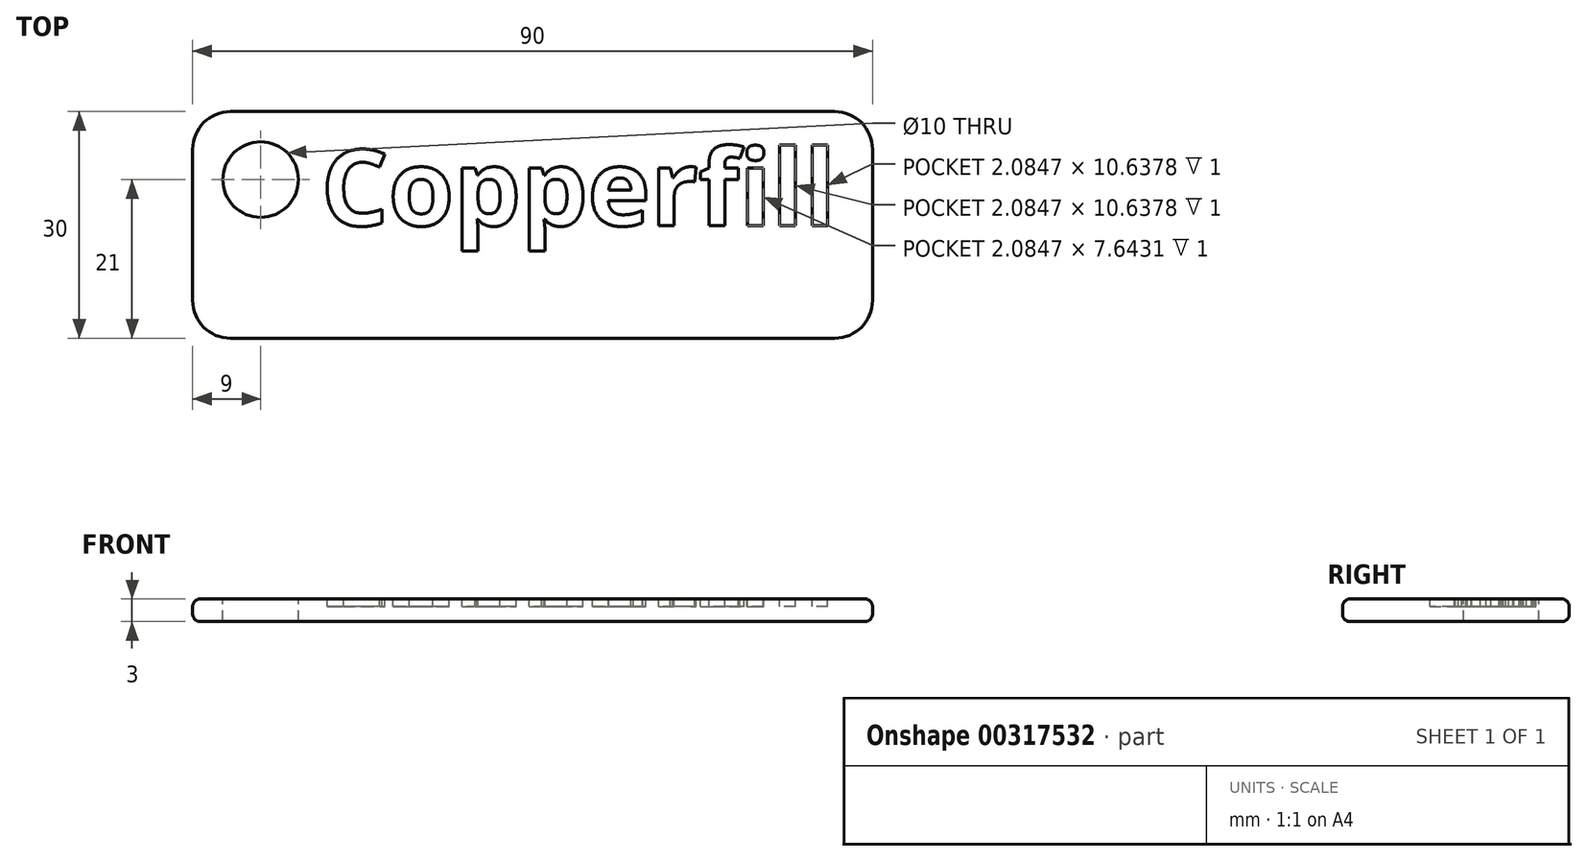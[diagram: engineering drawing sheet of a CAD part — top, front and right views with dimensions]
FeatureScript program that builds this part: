
annotation { "Feature Type Name" : "Feature", "Feature Type Description" : "" }
export const myFeature = defineFeature(function(context is Context, id is Id, definition is map)
    precondition{}
    {
        {
            var Q0;
            Q0=qCreatedBy(makeId("Top.planeOp"),FACE);
            var sketch = newSketch(context, id + "F0", { "sketchPlane" : qUnion([Q0])});
            skLineSegment(sketch, "E0.bottom", {"start": v(-45, 15) * mm, "end": v(45, 15) * mm});
            skLineSegment(sketch, "E0.top", {"start": v(-45, -15) * mm, "end": v(45, -15) * mm});
            skLineSegment(sketch, "E0.left", {"start": v(-45, 15) * mm, "end": v(-45, -15) * mm});
            skLineSegment(sketch, "E0.right", {"start": v(45, 15) * mm, "end": v(45, -15) * mm});
            skLineSegment(sketch, "E1", {"start": v(-45, 15) * mm, "end": v(45, -15) * mm, "construction": true});
            skSolve(sketch);
        }
        {
            var Q0;
            Q0=makeQuery(id+"F0.imprint","IMPRINT",FACE,{"disambiguationData":[TD([[makeQuery(id+"F0.imprint","IMPRINT",EDGE,{"derivedFrom":sQuery(id+"F0.wireOp",EDGE,"E0.bottom")}),-1.0]])]});
            extrude(context, id + "F1", {"entities" : qUnion([Q0]), "depth" : 3 * mm});
        }
        {
            var Q0;
            Q0=makeQuery(id+"F1.opExtrude","CAP_FACE",FACE,{"disambiguationData":[OSD([sQuery(id+"F0.wireOp",EDGE,"E0.bottom"),sQuery(id+"F0.wireOp",EDGE,"E0.top"),sQuery(id+"F0.wireOp",EDGE,"E0.left"),sQuery(id+"F0.wireOp",EDGE,"E0.right")])],"isStart":false});
            var Q1;
            Q1=makeQuery(id+"F1.opExtrude","CAP_FACE",FACE,{"disambiguationData":[OSD([sQuery(id+"F0.wireOp",EDGE,"E0.bottom"),sQuery(id+"F0.wireOp",EDGE,"E0.top"),sQuery(id+"F0.wireOp",EDGE,"E0.left"),sQuery(id+"F0.wireOp",EDGE,"E0.right")])],"isStart":true});
            fillet(context, id + "F2", {"entities" : qUnion([Q0, Q1]), "radius" : 1 * mm, "tangentPropagation" : true, "allowEdgeOverflow" : false});
        }
        {
            var Q0;
            Q0=makeQuery(id+"F1.opExtrude","SWEPT_EDGE",EDGE,{"disambiguationData":[OSD([sQuery(id+"F0.wireOp",EDGE,"E0.top"),sQuery(id+"F0.wireOp",EDGE,"E0.right")])]});
            var Q1;
            Q1=makeQuery(id+"F1.opExtrude","SWEPT_EDGE",EDGE,{"disambiguationData":[OSD([sQuery(id+"F0.wireOp",EDGE,"E0.bottom"),sQuery(id+"F0.wireOp",EDGE,"E0.right")])]});
            var Q2;
            Q2=makeQuery(id+"F1.opExtrude","SWEPT_EDGE",EDGE,{"disambiguationData":[OSD([sQuery(id+"F0.wireOp",EDGE,"E0.bottom"),sQuery(id+"F0.wireOp",EDGE,"E0.left")])]});
            var Q3;
            Q3=makeQuery(id+"F1.opExtrude","SWEPT_EDGE",EDGE,{"disambiguationData":[OSD([sQuery(id+"F0.wireOp",EDGE,"E0.top"),sQuery(id+"F0.wireOp",EDGE,"E0.left")])]});
            fillet(context, id + "F3", {"entities" : qUnion([Q0, Q1, Q2, Q3]), "radius" : 5 * mm, "tangentPropagation" : true, "allowEdgeOverflow" : false});
        }
        {
            var Q0;
            {var subQ0=sQuery(id+"F0.wireOp",EDGE,"E0.left");var subQ2=sQuery(id+"F0.wireOp",EDGE,"E0.bottom");var subQ4=sQuery(id+"F0.wireOp",EDGE,"E0.right");var subQ6=sQuery(id+"F0.wireOp",EDGE,"E0.top");Q0=makeQuery(id+"FmQCBBX3Ub0qneL_1.boolean.opBoolean","SPLIT",FACE,{"disambiguationData":[TD([makeQuery(id+"FmQCBBX3Ub0qneL_1.opExtrude","SWEPT_FACE",FACE,{"disambiguationData":[OSD([sQuery(id+"FOCoeRmDbjhRCuz_1.wireOp",EDGE,"4a1fb44a-e7be-4e23-9449-000d953c446c.sketch_text.stroke-0")])]})])],"derivedFrom":makeQuery(id+"F1.opExtrude","CAP_FACE",FACE,{"disambiguationData":[OSD([subQ2,subQ6,subQ0,subQ4])],"isStart":false})});}
            var sketch = newSketch(context, id + "F4", { "sketchPlane" : qUnion([Q0])});
            skCircle(sketch, "E2", {"center": v(-36, 6) * mm, "radius": 5 * mm});
            skSolve(sketch);
        }
        {
            var Q0;
            Q0=qSketchRegion(id+"F4",true);
            extrude(context, id + "F5", {"entities" : qUnion([Q0]), "operationType" : NewBodyOperationType.REMOVE, "oppositeDirection" : true, "depth" : 3 * mm});
        }
        {
            var Q0;
            Q0=makeQuery(id+"F1.opExtrude","CAP_FACE",FACE,{"disambiguationData":[OSD([sQuery(id+"F0.wireOp",EDGE,"E0.bottom"),sQuery(id+"F0.wireOp",EDGE,"E0.top"),sQuery(id+"F0.wireOp",EDGE,"E0.left"),sQuery(id+"F0.wireOp",EDGE,"E0.right")])],"isStart":false});
            var sketch = newSketch(context, id + "F6", { "sketchPlane" : qUnion([Q0])});
            skText(sketch, "E3", { "text": "Copperfill", "fontName": "OpenSans-Bold.ttf"});
            const initialGuessF6  = {"E3": [-0.028, -8e-05, 1, 0, 0.01008]};
            skSetInitialGuess(sketch, initialGuessF6);
            skSolve(sketch);
        }
        {
            var Q0;
            Q0=qSketchRegion(id+"F6",true);
            extrude(context, id + "F7", {"entities" : qUnion([Q0]), "operationType" : NewBodyOperationType.REMOVE, "oppositeDirection" : true, "depth" : 1 * mm});
        }
    });
